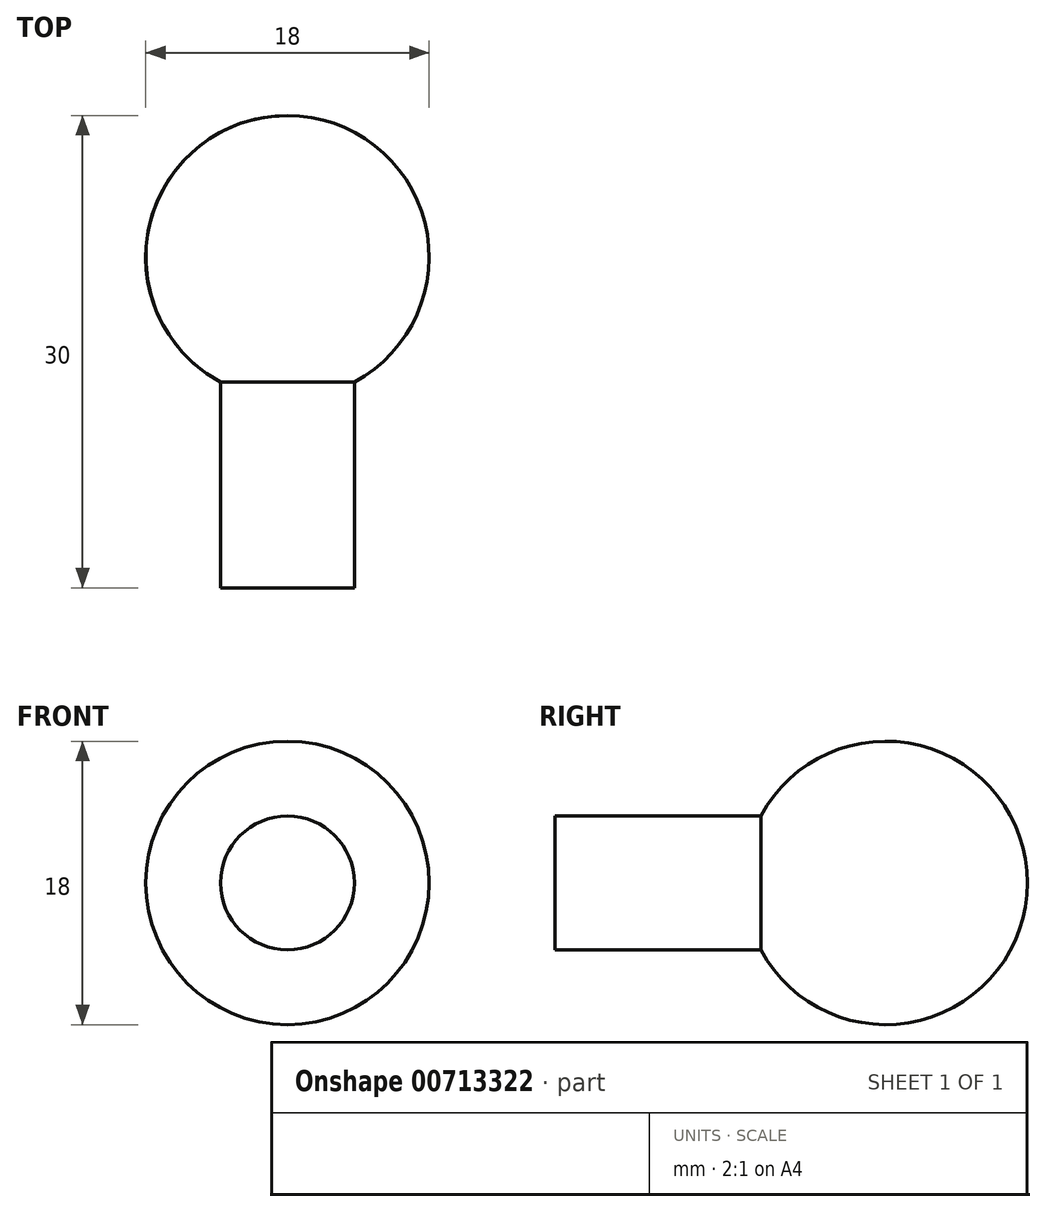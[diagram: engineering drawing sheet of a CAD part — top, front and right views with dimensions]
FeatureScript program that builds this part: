
annotation { "Feature Type Name" : "Feature", "Feature Type Description" : "" }
export const myFeature = defineFeature(function(context is Context, id is Id, definition is map)
    precondition{}
    {
        {
            var Q0;
            Q0=qCreatedBy(makeId("Top.planeOp"),FACE);
            var sketch = newSketch(context, id + "F0", { "sketchPlane" : qUnion([Q0])});
            skCircle(sketch, "E0", {"center": v(0, 0) * mm, "radius": 9 * mm});
            skLineSegment(sketch, "E1", {"start": v(-10.58, -40.3) * mm, "end": v(13.1, -40.3) * mm});
            skLineSegment(sketch, "E2", {"start": v(0, 0) * mm, "end": v(0, 9) * mm});
            skLineSegment(sketch, "E3", {"start": v(0, 9) * mm, "end": v(0, -9) * mm});
            skSolve(sketch);
        }
        {
            var Q0;
            {var subQ0=sQuery(id+"F0.wireOp",EDGE,"E3");var subQ4=makeQuery(id+"F0.imprint","IMPRINT",VERTEX,{"derivedFrom":subQ0});Q0=makeQuery(id+"F0.imprint","IMPRINT",FACE,{"disambiguationData":[TD([[makeQuery(id+"F0.imprint","IMPRINT",EDGE,{"disambiguationData":[TD([[subQ4,1.0]])],"derivedFrom":subQ0}),1.0]])]});}
            var Q1;
            Q1=sQuery(id+"F0.wireOp",EDGE,"E3");
            revolve(context, id + "F1", {"surfaceOperationType" : NewSurfaceOperationType.NEW, "entities" : qUnion([Q0]), "axis" : qUnion([Q1]), "revolveType" : RevolveType.FULL});
        }
        {
            var Q0;
            Q0=qCreatedBy(makeId("Front.planeOp"),FACE);
            var sketch = newSketch(context, id + "F2", { "sketchPlane" : qUnion([Q0])});
            skCircle(sketch, "E4", {"center": v(0, 0) * mm, "radius": 4.25 * mm});
            skSolve(sketch);
        }
        {
            var Q0;
            Q0 = qSketchRegion(id + "F2", true);
            extrude(context, id + "F3", {"entities" : qUnion([Q0]), "operationType" : NewBodyOperationType.ADD, "depth" : 21 * mm, "offsetDistance" : 25 * mm});
        }
    });
